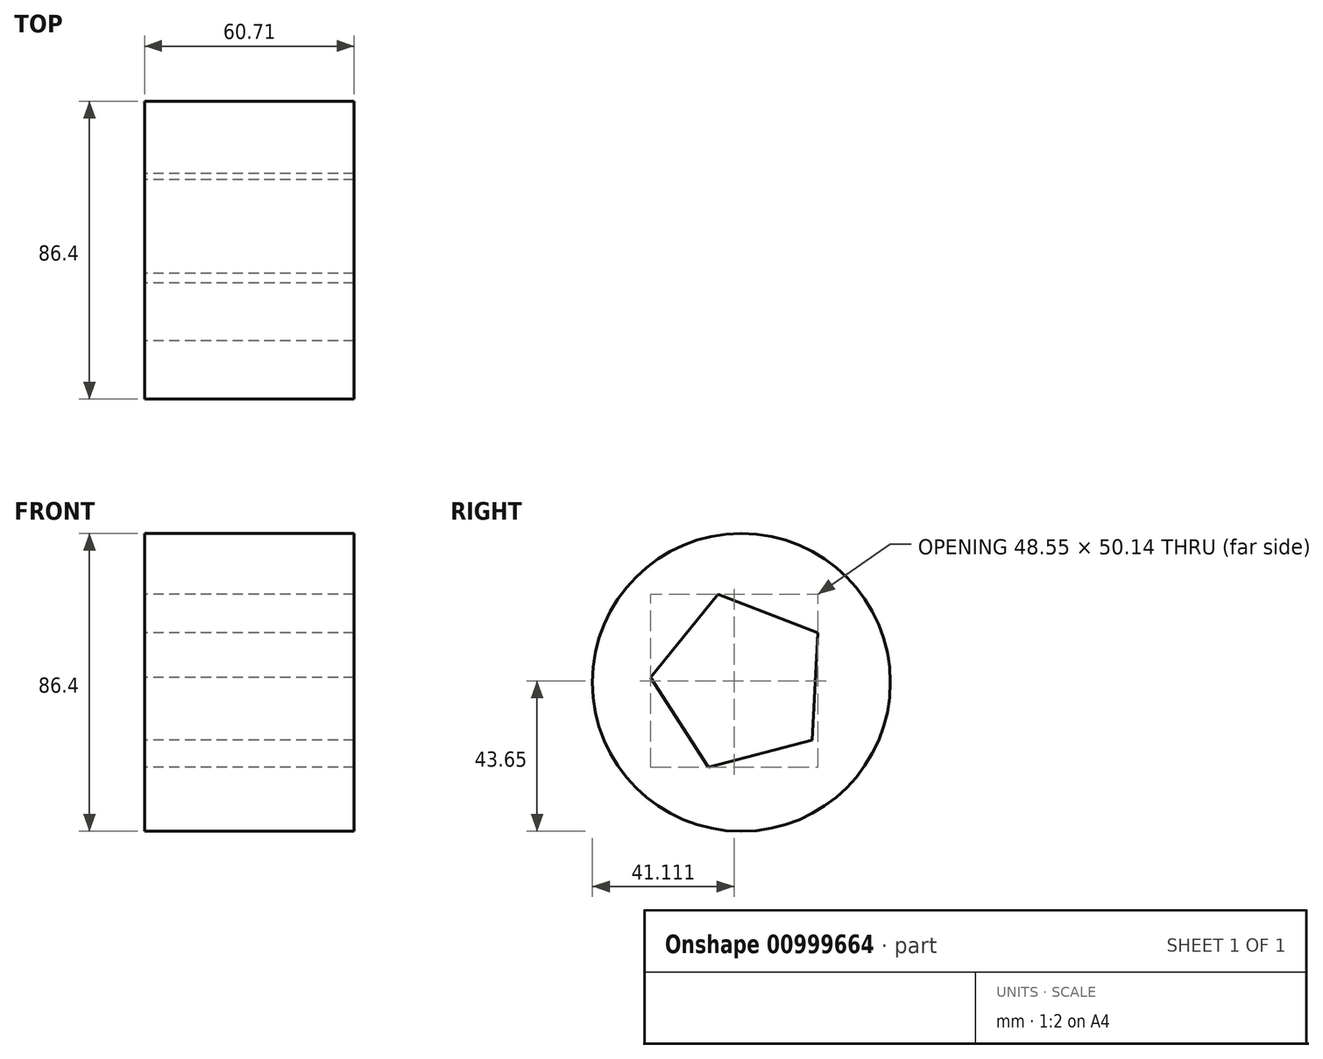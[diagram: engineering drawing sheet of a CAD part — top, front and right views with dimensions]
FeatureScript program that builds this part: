
annotation { "Feature Type Name" : "Feature", "Feature Type Description" : "" }
export const myFeature = defineFeature(function(context is Context, id is Id, definition is map)
    precondition{}
    {
        {
            var Q0;
            Q0=qCreatedBy(makeId("Right.planeOp"),FACE);
            var sketch = newSketch(context, id + "F0", { "sketchPlane" : qUnion([Q0])});
            skCircle(sketch, "E0", {"center": v(0, 0) * mm, "radius": 43.2 * mm});
            skSolve(sketch);
        }
        {
            var Q0;
            Q0=makeQuery(id+"F0.imprint","IMPRINT",FACE,{"disambiguationData":[TD([[makeQuery(id+"F0.imprint","IMPRINT",EDGE,{"derivedFrom":sQuery(id+"F0.wireOp",EDGE,"E0")}),1.0]])]});
            var sketch = newSketch(context, id + "F1", { "sketchPlane" : qUnion([Q0])});
            skCircle(sketch, "E1.cCircle", {"center": v(0, 0) * mm, "radius": 26.4 * mm, "construction": true});
            skLineSegment(sketch, "E1.0", {"start": v(22.18, 14.32) * mm, "end": v(20.47, -16.67) * mm});
            skLineSegment(sketch, "E1.1", {"start": v(20.47, -16.67) * mm, "end": v(-9.53, -24.62) * mm});
            skLineSegment(sketch, "E1.2", {"start": v(-9.53, -24.62) * mm, "end": v(-26.36, 1.46) * mm});
            skLineSegment(sketch, "E1.3", {"start": v(-26.36, 1.46) * mm, "end": v(-6.76, 25.52) * mm});
            skLineSegment(sketch, "E1.4", {"start": v(-6.76, 25.52) * mm, "end": v(22.18, 14.32) * mm});
            skSolve(sketch);
        }
        {
            var Q0;
            Q0=makeQuery(id+"F1.imprint","IMPRINT",FACE,{"disambiguationData":[TD([[makeQuery(id+"F1.imprint","IMPRINT",EDGE,{"derivedFrom":sQuery(id+"F1.wireOp",EDGE,"E1.0")}),1.0]])]});
            extrude(context, id + "F2", {"entities" : qUnion([Q0]), "depth" : 60.7 * mm, "offsetDistance" : 25.4 * mm});
        }
    });
